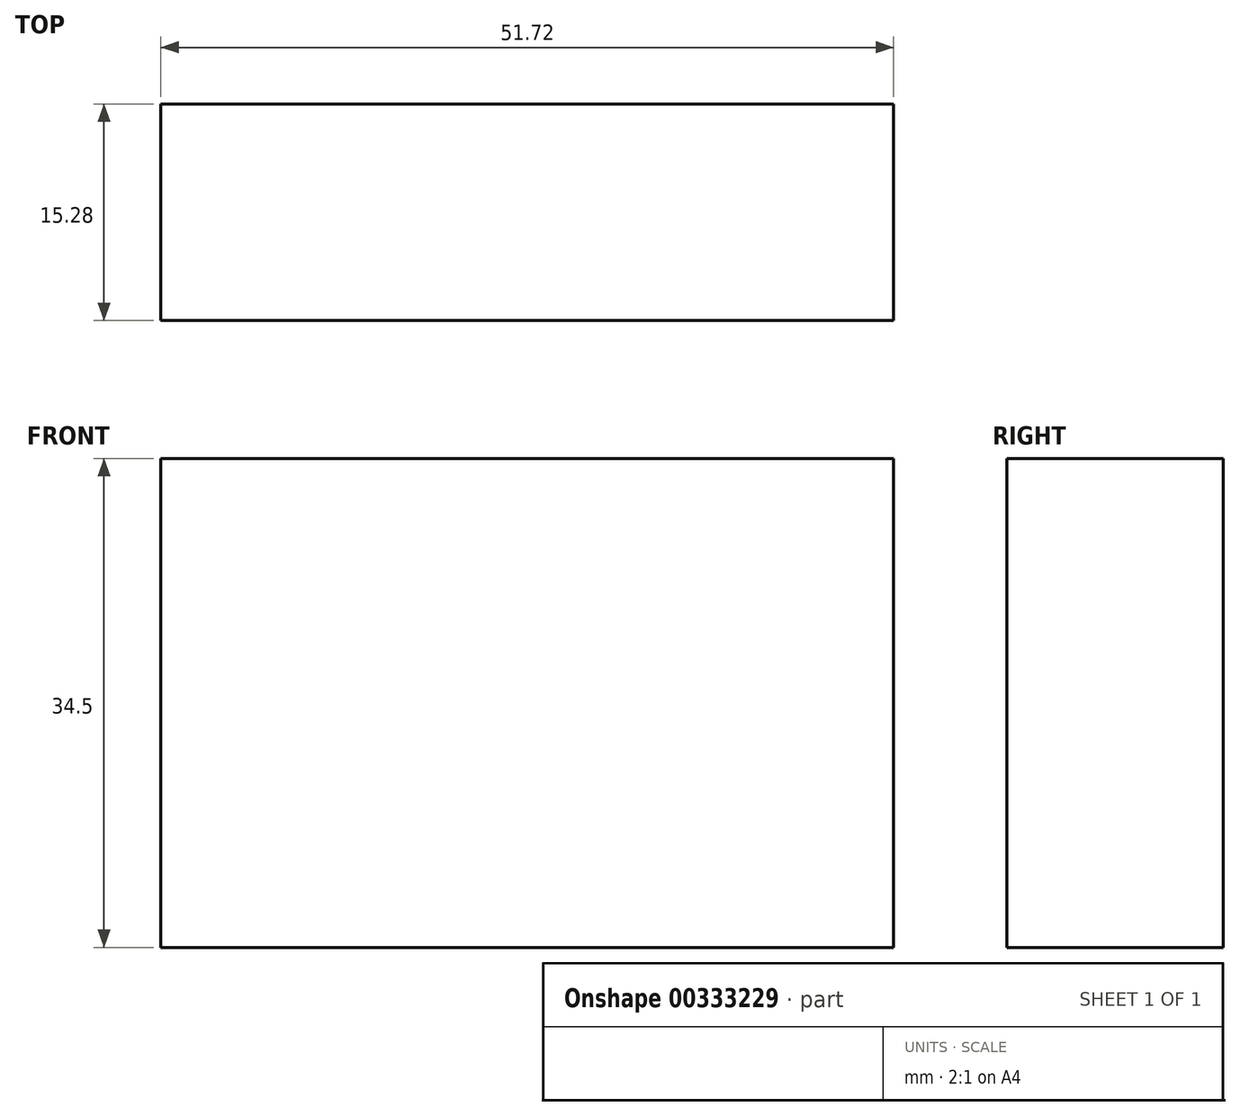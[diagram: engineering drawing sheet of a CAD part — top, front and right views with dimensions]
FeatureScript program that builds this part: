
annotation { "Feature Type Name" : "Feature", "Feature Type Description" : "" }
export const myFeature = defineFeature(function(context is Context, id is Id, definition is map)
    precondition{}
    {
        {
            var Q0;
            Q0=qCreatedBy(makeId("Front.planeOp"),FACE);
            var sketch = newSketch(context, id + "F0", { "sketchPlane" : qUnion([Q0])});
            skLineSegment(sketch, "E0.bottom", {"start": v(25.86, -17.25) * mm, "end": v(-25.86, -17.25) * mm});
            skLineSegment(sketch, "E0.top", {"start": v(25.86, 17.25) * mm, "end": v(-25.86, 17.25) * mm});
            skLineSegment(sketch, "E0.left", {"start": v(25.86, -17.25) * mm, "end": v(25.86, 17.25) * mm});
            skLineSegment(sketch, "E0.right", {"start": v(-25.86, -17.25) * mm, "end": v(-25.86, 17.25) * mm});
            skPoint(sketch, "E0.middle", {"position": v(0, 0) * mm});
            skSolve(sketch);
        }
        {
            var Q0;
            Q0=qSketchRegion(id+"F0",true);
            extrude(context, id + "F1", {"entities" : qUnion([Q0]), "depth" : 15.28 * mm});
        }
    });
